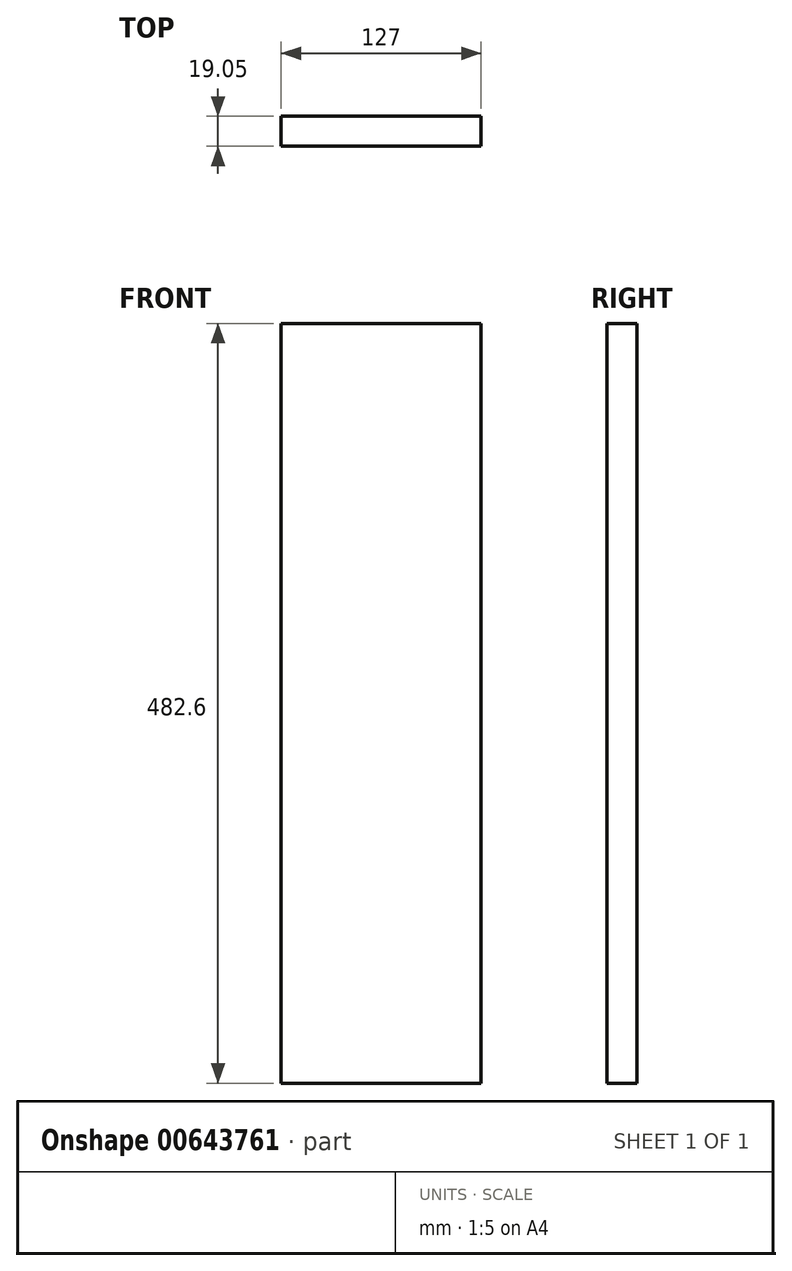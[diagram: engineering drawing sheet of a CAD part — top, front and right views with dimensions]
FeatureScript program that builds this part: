
annotation { "Feature Type Name" : "Feature", "Feature Type Description" : "" }
export const myFeature = defineFeature(function(context is Context, id is Id, definition is map)
    precondition{}
    {
        {
            var Q0;
            Q0=qCreatedBy(makeId("Front.planeOp"),FACE);
            var sketch = newSketch(context, id + "F0", { "sketchPlane" : qUnion([Q0])});
            skLineSegment(sketch, "E0.bottom", {"start": v(0, 0) * mm, "end": v(127, 0) * mm});
            skLineSegment(sketch, "E0.top", {"start": v(0, 482.6) * mm, "end": v(127, 482.6) * mm});
            skLineSegment(sketch, "E0.left", {"start": v(0, 0) * mm, "end": v(0, 482.6) * mm});
            skLineSegment(sketch, "E0.right", {"start": v(127, 0) * mm, "end": v(127, 482.6) * mm});
            skSolve(sketch);
        }
        {
            var Q0;
            Q0=makeQuery(id+"F0.imprint","IMPRINT",FACE,{"disambiguationData":[TD([[makeQuery(id+"F0.imprint","IMPRINT",EDGE,{"derivedFrom":sQuery(id+"F0.wireOp",EDGE,"E0.bottom")}),1.0]])]});
            extrude(context, id + "F1", {"entities" : qUnion([Q0]), "depth" : 19.05 * mm, "offsetDistance" : 25.4 * mm});
        }
    });
